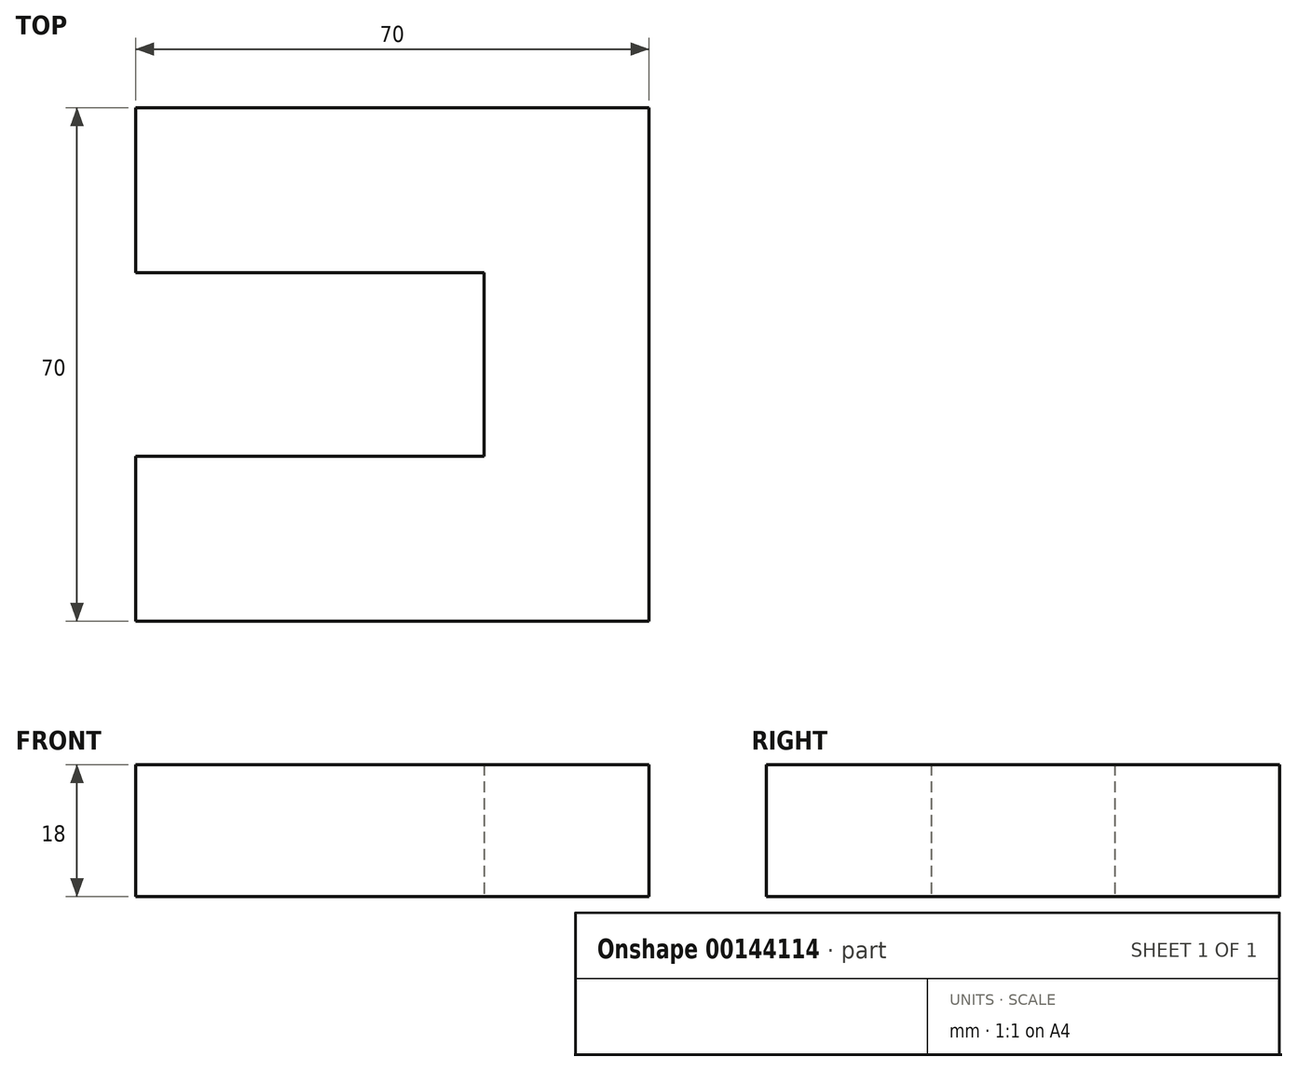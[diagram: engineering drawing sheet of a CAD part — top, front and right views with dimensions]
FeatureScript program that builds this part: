
annotation { "Feature Type Name" : "Feature", "Feature Type Description" : "" }
export const myFeature = defineFeature(function(context is Context, id is Id, definition is map)
    precondition{}
    {
        {
            var Q0;
            Q0=qCreatedBy(makeId("Top.planeOp"),FACE);
            var sketch = newSketch(context, id + "F0", { "sketchPlane" : qUnion([Q0])});
            skLineSegment(sketch, "E0", {"start": v(-70, 70) * mm, "end": v(0, 70) * mm});
            skLineSegment(sketch, "E1", {"start": v(0, 70) * mm, "end": v(0, 0) * mm});
            skLineSegment(sketch, "E2", {"start": v(0, 0) * mm, "end": v(-70, 0) * mm});
            skLineSegment(sketch, "E3", {"start": v(-70, 0) * mm, "end": v(-70, 22.5) * mm});
            skLineSegment(sketch, "E4", {"start": v(-70, 22.5) * mm, "end": v(-22.5, 22.5) * mm});
            skLineSegment(sketch, "E5", {"start": v(-22.5, 22.5) * mm, "end": v(-22.5, 47.5) * mm});
            skLineSegment(sketch, "E6", {"start": v(-22.5, 47.5) * mm, "end": v(-70, 47.5) * mm});
            skLineSegment(sketch, "E7", {"start": v(-70, 47.5) * mm, "end": v(-70, 70) * mm});
            skLineSegment(sketch, "E8", {"start": v(0, 35) * mm, "end": v(-22.5, 35) * mm, "construction": true});
            skSolve(sketch);
        }
        {
            var Q0;
            Q0=makeQuery(id+"F0.imprint","IMPRINT",FACE,{"disambiguationData":[TD([[makeQuery(id+"F0.imprint","IMPRINT",EDGE,{"derivedFrom":sQuery(id+"F0.wireOp",EDGE,"E0")}),-1.0]])]});
            extrude(context, id + "F1", {"entities" : qUnion([Q0]), "depth" : 18 * mm});
        }
    });
